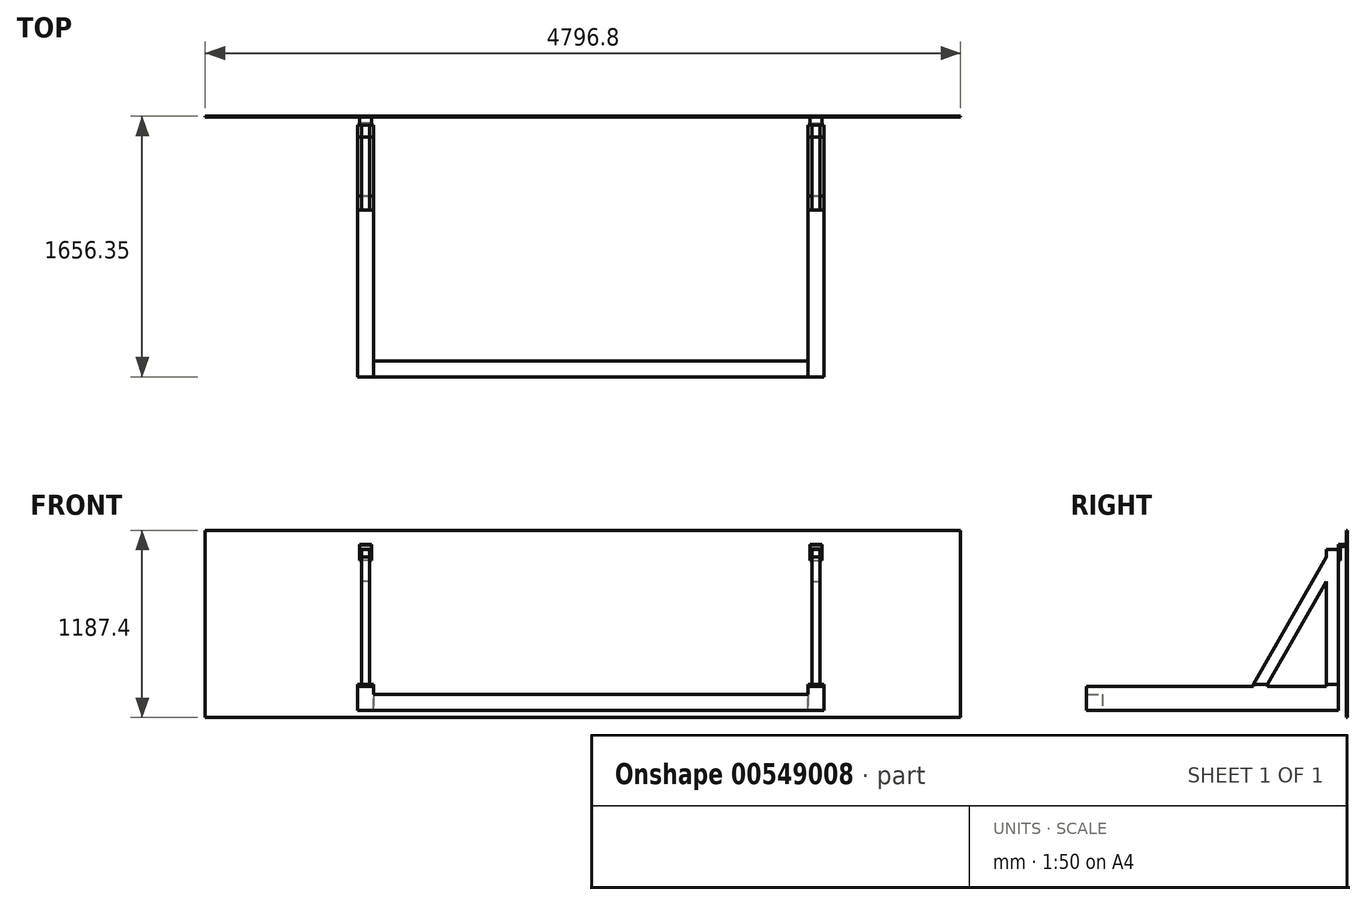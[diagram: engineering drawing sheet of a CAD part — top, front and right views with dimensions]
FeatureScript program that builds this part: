
annotation { "Feature Type Name" : "Feature", "Feature Type Description" : "" }
export const myFeature = defineFeature(function(context is Context, id is Id, definition is map)
    precondition{}
    {
        {
            var Q0;
            Q0=qCreatedBy(makeId("Right.planeOp"),FACE);
            var sketch = newSketch(context, id + "F0", { "sketchPlane" : qUnion([Q0])});
            skLineSegment(sketch, "E0.bottom", {"start": v(0, 160.17) * mm, "end": v(-37.3, 160.17) * mm});
            skLineSegment(sketch, "E0.top", {"start": v(0, 147.47) * mm, "end": v(-37.3, 147.47) * mm});
            skLineSegment(sketch, "E0.left", {"start": v(0, 160.17) * mm, "end": v(0, 147.47) * mm});
            skLineSegment(sketch, "E0.right", {"start": v(-37.3, 160.17) * mm, "end": v(-37.3, 147.47) * mm});
            skLineSegment(sketch, "E1.bottom", {"start": v(-37.3, 160.17) * mm, "end": v(-50, 160.17) * mm});
            skLineSegment(sketch, "E1.top", {"start": v(-37.3, 60.17) * mm, "end": v(-50, 60.17) * mm});
            skLineSegment(sketch, "E1.left", {"start": v(-37.3, 160.17) * mm, "end": v(-37.3, 60.17) * mm});
            skLineSegment(sketch, "E1.right", {"start": v(-50, 160.17) * mm, "end": v(-50, 60.17) * mm});
            skSolve(sketch);
        }
        {
            var Q0;
            {var subQ0=sQuery(id+"F0.wireOp",EDGE,"E0.bottom");Q0=makeQuery(id+"F0.imprint","IMPRINT",FACE,{"disambiguationData":[TD([[makeQuery(id+"F0.imprint","IMPRINT",EDGE,{"derivedFrom":subQ0}),1.0]])]});}
            var Q1;
            {var subQ3=sQuery(id+"F0.wireOp",EDGE,"E1.bottom");Q1=makeQuery(id+"F0.imprint","IMPRINT",FACE,{"disambiguationData":[TD([[makeQuery(id+"F0.imprint","IMPRINT",EDGE,{"derivedFrom":subQ3}),1.0]])]});}
            extrude(context, id + "F1", {"entities" : qUnion([Q0, Q1]), "depth" : 76.2 * mm, "offsetDistance" : 25 * mm});
        }
        {
            var Q0;
            Q0=makeQuery(id+"F1.opExtrude","SWEPT_FACE",FACE,{"disambiguationData":[OSD([sQuery(id+"F0.wireOp",EDGE,"E1.right")])]});
            var sketch = newSketch(context, id + "F2", { "sketchPlane" : qUnion([Q0])});
            skLineSegment(sketch, "E2.bottom", {"start": v(12.7, 130.17) * mm, "end": v(63.5, 130.17) * mm});
            skLineSegment(sketch, "E2.top", {"start": v(12.7, -727.13) * mm, "end": v(63.5, -727.13) * mm});
            skLineSegment(sketch, "E2.left", {"start": v(12.7, 130.17) * mm, "end": v(12.7, -727.13) * mm});
            skLineSegment(sketch, "E2.right", {"start": v(63.5, 130.17) * mm, "end": v(63.5, -727.13) * mm});
            skSolve(sketch);
        }
        {
            var Q0;
            {var subQ0=sQuery(id+"F2.wireOp",EDGE,"E2.top");Q0=makeQuery(id+"F2.imprint","IMPRINT",FACE,{"disambiguationData":[TD([[makeQuery(id+"F2.imprint","IMPRINT",EDGE,{"derivedFrom":subQ0}),1.0]])]});}
            var Q1;
            {var subQ0=sQuery(id+"F2.wireOp",EDGE,"E2.bottom");Q1=makeQuery(id+"F2.imprint","IMPRINT",FACE,{"disambiguationData":[TD([[makeQuery(id+"F2.imprint","IMPRINT",EDGE,{"derivedFrom":subQ0}),-1.0]])]});}
            extrude(context, id + "F3", {"entities" : qUnion([Q0, Q1]), "operationType" : NewBodyOperationType.ADD, "depth" : 76.2 * mm, "offsetDistance" : 25 * mm});
        }
        {
            var Q0;
            Q0=makeQuery(id+"F3.opExtrude","SWEPT_FACE",FACE,{"disambiguationData":[OSD([sQuery(id+"F2.wireOp",EDGE,"E2.top")])]});
            var sketch = newSketch(context, id + "F4", { "sketchPlane" : qUnion([Q0])});
            skLineSegment(sketch, "E3.bottom", {"start": v(-12.7, 126.2) * mm, "end": v(88.9, 126.2) * mm});
            skLineSegment(sketch, "E3.top", {"start": v(-12.7, 50) * mm, "end": v(88.9, 50) * mm});
            skLineSegment(sketch, "E3.left", {"start": v(-12.7, 126.2) * mm, "end": v(-12.7, 50) * mm});
            skLineSegment(sketch, "E3.right", {"start": v(88.9, 126.2) * mm, "end": v(88.9, 50) * mm});
            skSolve(sketch);
        }
        {
            var Q0;
            {var subQ2=sQuery(id+"F4.wireOp",EDGE,"E3.left");Q0=makeQuery(id+"F4.imprint","IMPRINT",FACE,{"disambiguationData":[TD([[makeQuery(id+"F4.imprint","IMPRINT",EDGE,{"derivedFrom":subQ2}),1.0]])]});}
            var Q1;
            {var subQ1=sQuery(id+"F2.wireOp",EDGE,"E2.top");var subQ2=makeQuery(id+"F3.opExtrude","SWEPT_EDGE",EDGE,{"disambiguationData":[OSD([subQ1,sQuery(id+"F2.wireOp",EDGE,"E2.left")])]});Q1=makeQuery(id+"F4.imprint","IMPRINT",FACE,{"disambiguationData":[TD([[makeQuery(id+"F4.imprint","IMPRINT",EDGE,{"derivedFrom":subQ2}),1.0]])]});}
            var Q2;
            {var subQ2=sQuery(id+"F4.wireOp",EDGE,"E3.right");Q2=makeQuery(id+"F4.imprint","IMPRINT",FACE,{"disambiguationData":[TD([[makeQuery(id+"F4.imprint","IMPRINT",EDGE,{"derivedFrom":subQ2}),-1.0]])]});}
            extrude(context, id + "F5", {"entities" : qUnion([Q0, Q1, Q2]), "operationType" : NewBodyOperationType.ADD, "depth" : 12.7 * mm, "offsetDistance" : 25 * mm});
        }
        {
            var Q0;
            Q0=makeQuery(id+"F3.opExtrude","SWEPT_FACE",FACE,{"disambiguationData":[OSD([sQuery(id+"F2.wireOp",EDGE,"E2.left")])]});
            var sketch = newSketch(context, id + "F6", { "sketchPlane" : qUnion([Q0])});
            skLineSegment(sketch, "E4", {"start": v(126.2, 80.17) * mm, "end": v(590, -727.13) * mm});
            skLineSegment(sketch, "E5", {"start": v(590, -727.13) * mm, "end": v(502.12, -727.13) * mm});
            skLineSegment(sketch, "E6", {"start": v(502.12, -727.13) * mm, "end": v(126.2, -72.8) * mm});
            skSolve(sketch);
        }
        {
            var Q0;
            {var subQ0=sQuery(id+"F6.wireOp",EDGE,"E4");Q0=makeQuery(id+"F6.imprint","IMPRINT",FACE,{"disambiguationData":[TD([[makeQuery(id+"F6.imprint","IMPRINT",EDGE,{"derivedFrom":subQ0}),-1.0]])]});}
            var Q1;
            Q1=makeQuery(id+"F3.opExtrude","SWEPT_FACE",FACE,{"disambiguationData":[OSD([sQuery(id+"F2.wireOp",EDGE,"E2.right")])]});
            extrude(context, id + "F7", {"entities" : qUnion([Q0]), "operationType" : NewBodyOperationType.ADD, "endBound" : BoundingType.UP_TO_SURFACE, "oppositeDirection" : true, "depth" : 25 * mm, "endBoundEntityFace" : qUnion([Q1]), "offsetDistance" : 25 * mm});
        }
        {
            var Q0;
            Q0=makeQuery(id+"F7.opExtrude","SWEPT_FACE",FACE,{"disambiguationData":[OSD([sQuery(id+"F6.wireOp",EDGE,"E5")])]});
            var sketch = newSketch(context, id + "F8", { "sketchPlane" : qUnion([Q0])});
            skLineSegment(sketch, "E7.bottom", {"start": v(-12.7, 590) * mm, "end": v(88.9, 590) * mm});
            skLineSegment(sketch, "E7.top", {"start": v(-12.7, 502.12) * mm, "end": v(88.9, 502.12) * mm});
            skLineSegment(sketch, "E7.left", {"start": v(-12.7, 590) * mm, "end": v(-12.7, 502.12) * mm});
            skLineSegment(sketch, "E7.right", {"start": v(88.9, 590) * mm, "end": v(88.9, 502.12) * mm});
            skSolve(sketch);
        }
        {
            var Q0;
            {var subQ2=sQuery(id+"F8.wireOp",EDGE,"E7.left");Q0=makeQuery(id+"F8.imprint","IMPRINT",FACE,{"disambiguationData":[TD([[makeQuery(id+"F8.imprint","IMPRINT",EDGE,{"derivedFrom":subQ2}),1.0]])]});}
            var Q1;
            {var subQ1=sQuery(id+"F6.wireOp",EDGE,"E5");var subQ3=makeQuery(id+"F7.opExtrude","CAP_EDGE",EDGE,{"disambiguationData":[OSD([subQ1])],"isStart":true});Q1=makeQuery(id+"F8.imprint","IMPRINT",FACE,{"disambiguationData":[TD([[makeQuery(id+"F8.imprint","IMPRINT",EDGE,{"derivedFrom":subQ3}),1.0]])]});}
            var Q2;
            {var subQ2=sQuery(id+"F8.wireOp",EDGE,"E7.right");Q2=makeQuery(id+"F8.imprint","IMPRINT",FACE,{"disambiguationData":[TD([[makeQuery(id+"F8.imprint","IMPRINT",EDGE,{"derivedFrom":subQ2}),-1.0]])]});}
            extrude(context, id + "F9", {"entities" : qUnion([Q0, Q1, Q2]), "operationType" : NewBodyOperationType.ADD, "depth" : 12.7 * mm, "offsetDistance" : 25 * mm});
        }
        {
            var Q0;
            Q0=makeQuery(id+"F5.boolean.opBoolean","MERGE",FACE,{"derivedFrom":[makeQuery(id+"F3.opExtrude","CAP_FACE",FACE,{"disambiguationData":[OSD([sQuery(id+"F2.wireOp",EDGE,"E2.bottom"),sQuery(id+"F2.wireOp",EDGE,"E2.top"),sQuery(id+"F2.wireOp",EDGE,"E2.left"),sQuery(id+"F2.wireOp",EDGE,"E2.right")])],"isStart":true}),makeQuery(id+"F5.opExtrude","SWEPT_FACE",FACE,{"disambiguationData":[OSD([sQuery(id+"F4.wireOp",EDGE,"E3.top")])]})]});
            var sketch = newSketch(context, id + "F10", { "sketchPlane" : qUnion([Q0])});
            skLineSegment(sketch, "E8.bottom", {"start": v(-88.9, -739.83) * mm, "end": v(12.7, -739.83) * mm});
            skLineSegment(sketch, "E8.top", {"start": v(-88.9, -892.23) * mm, "end": v(12.7, -892.23) * mm});
            skLineSegment(sketch, "E8.left", {"start": v(-88.9, -739.83) * mm, "end": v(-88.9, -892.23) * mm});
            skLineSegment(sketch, "E8.right", {"start": v(12.7, -739.83) * mm, "end": v(12.7, -892.23) * mm});
            skSolve(sketch);
        }
        {
            var Q0;
            Q0=makeQuery(id+"F10.imprint","IMPRINT",FACE,{"disambiguationData":[TD([[makeQuery(id+"F10.imprint","IMPRINT",EDGE,{"derivedFrom":sQuery(id+"F10.wireOp",EDGE,"E8.bottom")}),1.0]])]});
            extrude(context, id + "F11", {"entities" : qUnion([Q0]), "operationType" : NewBodyOperationType.ADD, "oppositeDirection" : true, "depth" : 1600 * mm, "offsetDistance" : 25 * mm});
        }
        {
            var Q0;
            Q0=makeQuery(id+"F11.boolean.opBoolean","MERGE",FACE,{"derivedFrom":[makeQuery(id+"F5.opExtrude","SWEPT_FACE",FACE,{"disambiguationData":[OSD([sQuery(id+"F4.wireOp",EDGE,"E3.right")])]}),makeQuery(id+"F9.opExtrude","SWEPT_FACE",FACE,{"disambiguationData":[OSD([sQuery(id+"F8.wireOp",EDGE,"E7.right")])]}),makeQuery(id+"F11.opExtrude","SWEPT_FACE",FACE,{"disambiguationData":[OSD([sQuery(id+"F10.wireOp",EDGE,"E8.left")])]})]});
            var sketch = newSketch(context, id + "F12", { "sketchPlane" : qUnion([Q0])});
            skLineSegment(sketch, "E9.bottom", {"start": v(-1650, -790.63) * mm, "end": v(-1548.4, -790.63) * mm});
            skLineSegment(sketch, "E9.top", {"start": v(-1650, -892.23) * mm, "end": v(-1548.4, -892.23) * mm});
            skLineSegment(sketch, "E9.left", {"start": v(-1650, -790.63) * mm, "end": v(-1650, -892.23) * mm});
            skLineSegment(sketch, "E9.right", {"start": v(-1548.4, -790.63) * mm, "end": v(-1548.4, -892.23) * mm});
            skSolve(sketch);
        }
        {
            var Q0;
            Q0=makeQuery(id+"F12.imprint","IMPRINT",FACE,{"disambiguationData":[TD([[makeQuery(id+"F12.imprint","IMPRINT",EDGE,{"derivedFrom":sQuery(id+"F12.wireOp",EDGE,"E9.bottom")}),-1.0]])]});
            extrude(context, id + "F13", {"entities" : qUnion([Q0]), "operationType" : NewBodyOperationType.ADD, "depth" : (2860 * mm - 101.6 * mm) / 2, "offsetDistance" : 25 * mm});
        }
        {
            var Q0;
            Q0=makeQuery(id+"F1.opExtrude","SWEPT_BODY",BODY,{"disambiguationData":[OSD([sQuery(id+"F0.wireOp",EDGE,"E0.bottom"),sQuery(id+"F0.wireOp",EDGE,"E0.top"),sQuery(id+"F0.wireOp",EDGE,"E0.left"),sQuery(id+"F0.wireOp",EDGE,"E1.bottom"),sQuery(id+"F0.wireOp",EDGE,"E1.top"),sQuery(id+"F0.wireOp",EDGE,"E1.left"),sQuery(id+"F0.wireOp",EDGE,"E1.right")])]});
            var Q1;
            Q1=makeQuery(id+"F13.opExtrude","CAP_FACE",FACE,{"disambiguationData":[OSD([sQuery(id+"F12.wireOp",EDGE,"E9.bottom"),sQuery(id+"F12.wireOp",EDGE,"E9.top"),sQuery(id+"F12.wireOp",EDGE,"E9.left"),sQuery(id+"F12.wireOp",EDGE,"E9.right")])],"isStart":false});
            mirror(context, id + "F14", {"operationType" : NewBodyOperationType.ADD, "entities" : qUnion([Q0]), "mirrorPlane" : qUnion([Q1])});
        }
        {
            var Q0;
            Q0=makeQuery(id+"F1.opExtrude","SWEPT_FACE",FACE,{"disambiguationData":[OSD([sQuery(id+"F0.wireOp",EDGE,"E0.left")])]});
            var sketch = newSketch(context, id + "F15", { "sketchPlane" : qUnion([Q0])});
            skLineSegment(sketch, "E10.bottom", {"start": v(-3816.3, 250.17) * mm, "end": v(980.5, 250.17) * mm});
            skLineSegment(sketch, "E10.top", {"start": v(-3816.3, -937.23) * mm, "end": v(980.5, -937.23) * mm});
            skLineSegment(sketch, "E10.left", {"start": v(-3816.3, 250.17) * mm, "end": v(-3816.3, -937.23) * mm});
            skLineSegment(sketch, "E10.right", {"start": v(980.5, 250.17) * mm, "end": v(980.5, -937.23) * mm});
            skLineSegment(sketch, "E11.0", {"start": v(-2936.2, 160.17) * mm, "end": v(-2936.2, 147.47) * mm});
            skSolve(sketch);
        }
        {
            var Q0;
            Q0=makeQuery(id+"F15.imprint","IMPRINT",FACE,{"disambiguationData":[TD([[makeQuery(id+"F15.imprint","IMPRINT",EDGE,{"derivedFrom":sQuery(id+"F15.wireOp",EDGE,"E10.bottom")}),-1.0]])]});
            var Q1;
            {var subQ0=sQuery(id+"F0.wireOp",EDGE,"E0.left");Q1=makeQuery(id+"F15.imprint","IMPRINT",FACE,{"disambiguationData":[TD([[makeQuery(id+"F15.imprint","IMPRINT",EDGE,{"derivedFrom":makeQuery(id+"F1.opExtrude","CAP_EDGE",EDGE,{"disambiguationData":[OSD([subQ0])],"isStart":true})}),-1.0]])]});}
            extrude(context, id + "F16", {"entities" : qUnion([Q0, Q1]), "operationType" : NewBodyOperationType.ADD, "depth" : 6.35 * mm, "offsetDistance" : 25 * mm});
        }
    });
